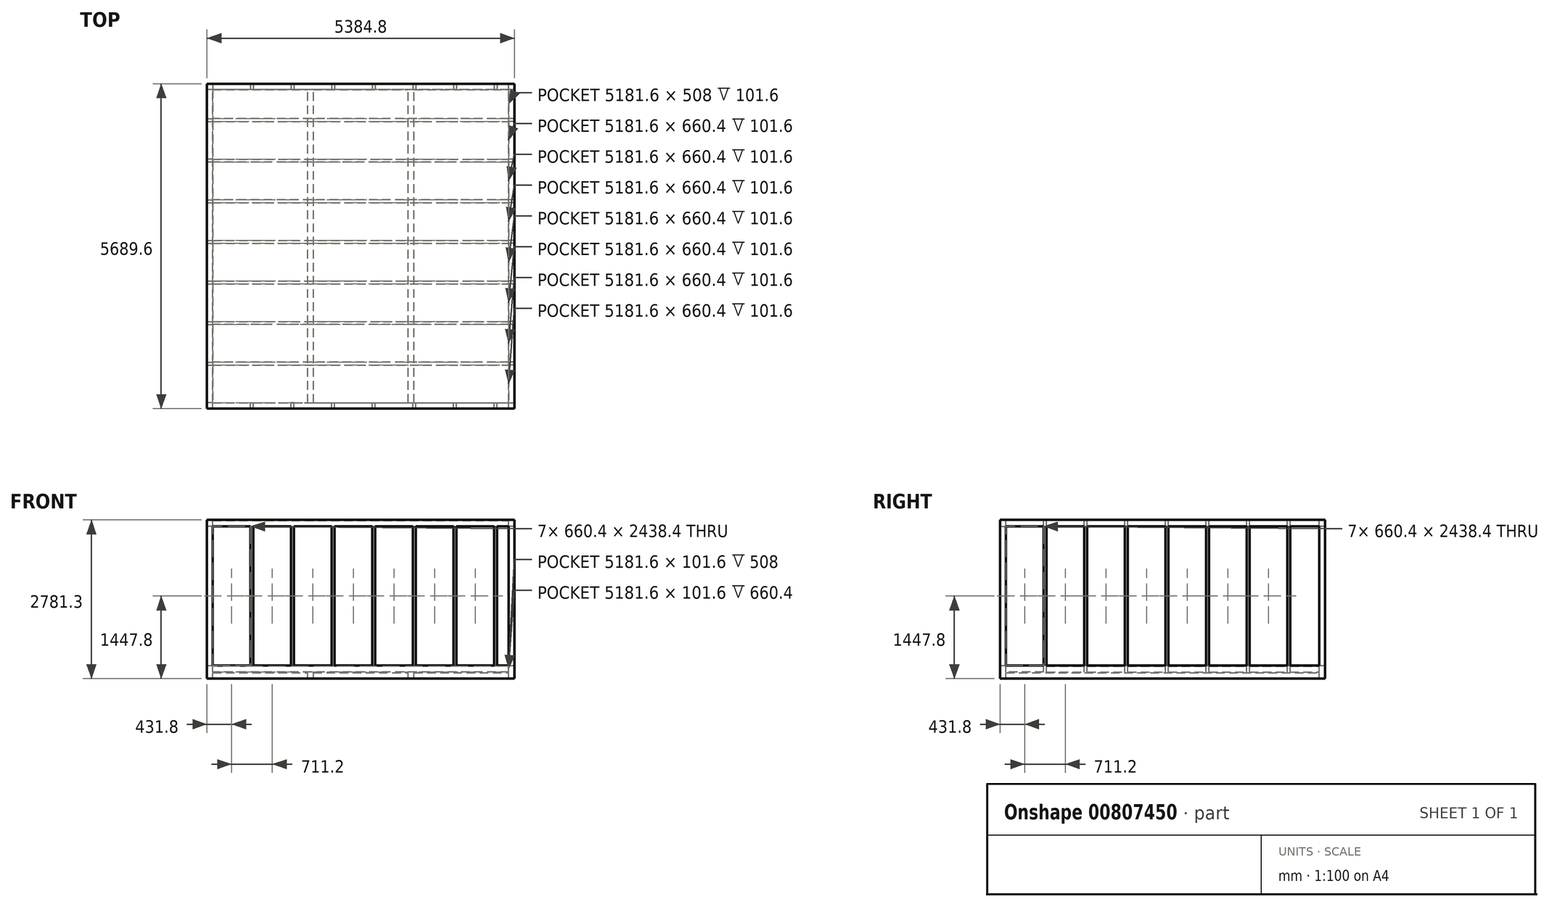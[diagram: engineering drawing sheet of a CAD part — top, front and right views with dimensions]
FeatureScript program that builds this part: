
annotation { "Feature Type Name" : "Feature", "Feature Type Description" : "" }
export const myFeature = defineFeature(function(context is Context, id is Id, definition is map)
    precondition{}
    {
        {
            var Q0;
            Q0=qCreatedBy(makeId("Top.planeOp"),FACE);
            var sketch = newSketch(context, id + "F0", { "sketchPlane" : qUnion([Q0])});
            skLineSegment(sketch, "E0.bottom", {"start": v(0, 0) * mm, "end": v(-5384.8, 0) * mm});
            skLineSegment(sketch, "E0.top", {"start": v(0, 5689.6) * mm, "end": v(-5384.8, 5689.6) * mm});
            skLineSegment(sketch, "E0.left", {"start": v(0, 0) * mm, "end": v(0, 5689.6) * mm});
            skLineSegment(sketch, "E0.right", {"start": v(-5384.8, 0) * mm, "end": v(-5384.8, 5689.6) * mm});
            skLineSegment(sketch, "E1", {"start": v(-5384.8, 0) * mm, "end": v(-5283.2, 0) * mm});
            skLineSegment(sketch, "E2", {"start": v(-5283.2, 0) * mm, "end": v(-5384.8, 0) * mm});
            skLineSegment(sketch, "E3", {"start": v(-5384.8, 0) * mm, "end": v(-5384.8, 101.6) * mm});
            skLineSegment(sketch, "E4", {"start": v(-5384.8, 101.6) * mm, "end": v(-5384.8, 5588) * mm});
            skLineSegment(sketch, "E5", {"start": v(-5384.8, 5588) * mm, "end": v(-5283.2, 5588) * mm});
            skLineSegment(sketch, "E6", {"start": v(-5283.2, 5588) * mm, "end": v(-101.6, 5588) * mm});
            skSolve(sketch);
        }
        {
            var Q0;
            Q0 = qSketchRegion(id + "F0", true);
            extrude(context, id + "F1", {"entities" : qUnion([Q0]), "depth" : 101.6 * mm, "offsetDistance" : 25.4 * mm});
        }
        {
            var Q0;
            Q0=makeQuery(id+"F1.opExtrude","CAP_FACE",FACE,{"disambiguationData":[OSD([sQuery(id+"F0.wireOp",EDGE,"E0.bottom"),sQuery(id+"F0.wireOp",EDGE,"E0.top"),sQuery(id+"F0.wireOp",EDGE,"E0.left"),sQuery(id+"F0.wireOp",EDGE,"E0.right"),sQuery(id+"F0.wireOp",EDGE,"E2"),sQuery(id+"F0.wireOp",EDGE,"E3"),sQuery(id+"F0.wireOp",EDGE,"E4")])],"isStart":false});
            var sketch = newSketch(context, id + "F2", { "sketchPlane" : qUnion([Q0])});
            skLineSegment(sketch, "E7", {"start": v(-5384.8, 0) * mm, "end": v(-5283.2, 0) * mm});
            skLineSegment(sketch, "E8", {"start": v(-5283.2, 0) * mm, "end": v(-3624.58, 0) * mm});
            skLineSegment(sketch, "E9", {"start": v(-3624.58, 0) * mm, "end": v(-3522.98, 0) * mm});
            skLineSegment(sketch, "E10", {"start": v(-3522.98, 0) * mm, "end": v(-1861.82, 0) * mm});
            skLineSegment(sketch, "E11", {"start": v(-1861.82, 0) * mm, "end": v(-1760.22, 0) * mm});
            skLineSegment(sketch, "E12", {"start": v(-1760.22, 0) * mm, "end": v(-101.6, 0) * mm});
            skLineSegment(sketch, "E13", {"start": v(-101.6, 0) * mm, "end": v(0, 0) * mm});
            skLineSegment(sketch, "E14", {"start": v(0, 0) * mm, "end": v(0, 101.6) * mm});
            skLineSegment(sketch, "E15", {"start": v(0, 101.6) * mm, "end": v(0, 1861.82) * mm});
            skLineSegment(sketch, "E16", {"start": v(0, 1861.82) * mm, "end": v(0, 1963.42) * mm});
            skLineSegment(sketch, "E17", {"start": v(0, 1963.42) * mm, "end": v(0, 3726.18) * mm});
            skLineSegment(sketch, "E18", {"start": v(0, 3726.18) * mm, "end": v(0, 3827.78) * mm});
            skLineSegment(sketch, "E19", {"start": v(0, 3827.78) * mm, "end": v(0, 5588) * mm});
            skLineSegment(sketch, "E20", {"start": v(0, 5588) * mm, "end": v(0, 5689.6) * mm});
            skLineSegment(sketch, "E21.bottom", {"start": v(-5283.2, 101.6) * mm, "end": v(-3624.58, 101.6) * mm});
            skLineSegment(sketch, "E21.top", {"start": v(-5283.2, 5588) * mm, "end": v(-3624.58, 5588) * mm});
            skLineSegment(sketch, "E21.left", {"start": v(-5283.2, 101.6) * mm, "end": v(-5283.2, 5588) * mm});
            skLineSegment(sketch, "E21.right", {"start": v(-3624.58, 101.6) * mm, "end": v(-3624.58, 5588) * mm});
            skLineSegment(sketch, "E22.bottom", {"start": v(-3522.98, 101.6) * mm, "end": v(-1861.82, 101.6) * mm});
            skLineSegment(sketch, "E22.top", {"start": v(-3522.98, 5588) * mm, "end": v(-1861.82, 5588) * mm});
            skLineSegment(sketch, "E22.left", {"start": v(-3522.98, 101.6) * mm, "end": v(-3522.98, 5588) * mm});
            skLineSegment(sketch, "E22.right", {"start": v(-1861.82, 101.6) * mm, "end": v(-1861.82, 5588) * mm});
            skLineSegment(sketch, "E23.bottom", {"start": v(-1760.22, 101.6) * mm, "end": v(-101.6, 101.6) * mm});
            skLineSegment(sketch, "E23.top", {"start": v(-1760.22, 5588) * mm, "end": v(-101.6, 5588) * mm});
            skLineSegment(sketch, "E23.left", {"start": v(-1760.22, 101.6) * mm, "end": v(-1760.22, 5588) * mm});
            skLineSegment(sketch, "E23.right", {"start": v(-101.6, 101.6) * mm, "end": v(-101.6, 5588) * mm});
            skSolve(sketch);
        }
        {
            var Q0;
            Q0 = qSketchRegion(id + "F2", true);
            extrude(context, id + "F3", {"entities" : qUnion([Q0]), "operationType" : NewBodyOperationType.REMOVE, "oppositeDirection" : true, "depth" : 101.6 * mm, "offsetDistance" : 25.4 * mm});
        }
        {
            var Q0;
            Q0=makeQuery(id+"F1.opExtrude","CAP_FACE",FACE,{"disambiguationData":[OSD([sQuery(id+"F0.wireOp",EDGE,"E0.bottom"),sQuery(id+"F0.wireOp",EDGE,"E0.top"),sQuery(id+"F0.wireOp",EDGE,"E0.left"),sQuery(id+"F0.wireOp",EDGE,"E0.right"),sQuery(id+"F0.wireOp",EDGE,"E2"),sQuery(id+"F0.wireOp",EDGE,"E3"),sQuery(id+"F0.wireOp",EDGE,"E4")])],"isStart":false});
            var sketch = newSketch(context, id + "F4", { "sketchPlane" : qUnion([Q0])});
            skLineSegment(sketch, "E24.bottom", {"start": v(-5384.8, 0) * mm, "end": v(0, 0) * mm});
            skLineSegment(sketch, "E24.top", {"start": v(-5384.8, 5689.6) * mm, "end": v(0, 5689.6) * mm});
            skLineSegment(sketch, "E24.left", {"start": v(-5384.8, 0) * mm, "end": v(-5384.8, 5689.6) * mm});
            skLineSegment(sketch, "E24.right", {"start": v(0, 0) * mm, "end": v(0, 5689.6) * mm});
            skSolve(sketch);
        }
        {
            var Q0;
            Q0 = qSketchRegion(id + "F4", true);
            extrude(context, id + "F5", {"entities" : qUnion([Q0]), "operationType" : NewBodyOperationType.ADD, "depth" : 114.3 * mm, "offsetDistance" : 25.4 * mm});
        }
        {
            var Q0;
            Q0=makeQuery(id+"F5.opExtrude","CAP_FACE",FACE,{"disambiguationData":[OSD([sQuery(id+"F4.wireOp",EDGE,"E24.bottom"),sQuery(id+"F4.wireOp",EDGE,"E24.top"),sQuery(id+"F4.wireOp",EDGE,"E24.left"),sQuery(id+"F4.wireOp",EDGE,"E24.right")])],"isStart":false});
            var sketch = newSketch(context, id + "F6", { "sketchPlane" : qUnion([Q0])});
            skLineSegment(sketch, "E25", {"start": v(-5384.8, 0) * mm, "end": v(-5283.2, 0) * mm});
            skLineSegment(sketch, "E26", {"start": v(-5283.2, 0) * mm, "end": v(-101.6, 0) * mm});
            skLineSegment(sketch, "E27", {"start": v(-101.6, 0) * mm, "end": v(0, 0) * mm});
            skLineSegment(sketch, "E28", {"start": v(0, 0) * mm, "end": v(0, 101.6) * mm});
            skLineSegment(sketch, "E29", {"start": v(0, 101.6) * mm, "end": v(0, 762) * mm});
            skLineSegment(sketch, "E30", {"start": v(0, 762) * mm, "end": v(0, 812.8) * mm});
            skLineSegment(sketch, "E31", {"start": v(0, 812.8) * mm, "end": v(0, 1473.2) * mm});
            skLineSegment(sketch, "E32", {"start": v(0, 1473.2) * mm, "end": v(0, 1524) * mm});
            skLineSegment(sketch, "E33", {"start": v(0, 1524) * mm, "end": v(0, 2184.4) * mm});
            skLineSegment(sketch, "E34", {"start": v(0, 2184.4) * mm, "end": v(0, 2235.2) * mm});
            skLineSegment(sketch, "E35", {"start": v(0, 2235.2) * mm, "end": v(0, 2895.6) * mm});
            skLineSegment(sketch, "E36", {"start": v(0, 2895.6) * mm, "end": v(0, 2946.4) * mm});
            skLineSegment(sketch, "E37", {"start": v(0, 2946.4) * mm, "end": v(0, 3606.8) * mm});
            skLineSegment(sketch, "E38", {"start": v(0, 3606.8) * mm, "end": v(0, 3657.6) * mm});
            skLineSegment(sketch, "E39", {"start": v(0, 3657.6) * mm, "end": v(0, 4318) * mm});
            skLineSegment(sketch, "E40", {"start": v(0, 4318) * mm, "end": v(0, 4368.8) * mm});
            skLineSegment(sketch, "E41", {"start": v(0, 4368.8) * mm, "end": v(0, 5029.2) * mm});
            skLineSegment(sketch, "E42", {"start": v(0, 5029.2) * mm, "end": v(0, 5080) * mm});
            skLineSegment(sketch, "E43", {"start": v(0, 5080) * mm, "end": v(0, 5588) * mm});
            skLineSegment(sketch, "E44", {"start": v(0, 5588) * mm, "end": v(0, 5689.6) * mm});
            skLineSegment(sketch, "E45.bottom", {"start": v(-101.6, 762) * mm, "end": v(-5283.2, 762) * mm});
            skLineSegment(sketch, "E45.top", {"start": v(-101.6, 101.6) * mm, "end": v(-5283.2, 101.6) * mm});
            skLineSegment(sketch, "E45.left", {"start": v(-101.6, 762) * mm, "end": v(-101.6, 101.6) * mm});
            skLineSegment(sketch, "E45.right", {"start": v(-5283.2, 762) * mm, "end": v(-5283.2, 101.6) * mm});
            skLineSegment(sketch, "E46.bottom", {"start": v(-101.6, 812.8) * mm, "end": v(-5283.2, 812.8) * mm});
            skLineSegment(sketch, "E46.top", {"start": v(-101.6, 1473.2) * mm, "end": v(-5283.2, 1473.2) * mm});
            skLineSegment(sketch, "E46.left", {"start": v(-101.6, 812.8) * mm, "end": v(-101.6, 1473.2) * mm});
            skLineSegment(sketch, "E46.right", {"start": v(-5283.2, 812.8) * mm, "end": v(-5283.2, 1473.2) * mm});
            skLineSegment(sketch, "E47.bottom", {"start": v(-101.6, 1524) * mm, "end": v(-5283.2, 1524) * mm});
            skLineSegment(sketch, "E47.top", {"start": v(-101.6, 2184.4) * mm, "end": v(-5283.2, 2184.4) * mm});
            skLineSegment(sketch, "E47.left", {"start": v(-101.6, 1524) * mm, "end": v(-101.6, 2184.4) * mm});
            skLineSegment(sketch, "E47.right", {"start": v(-5283.2, 1524) * mm, "end": v(-5283.2, 2184.4) * mm});
            skLineSegment(sketch, "E48.bottom", {"start": v(-101.6, 2235.2) * mm, "end": v(-5283.2, 2235.2) * mm});
            skLineSegment(sketch, "E48.top", {"start": v(-101.6, 2895.6) * mm, "end": v(-5283.2, 2895.6) * mm});
            skLineSegment(sketch, "E48.left", {"start": v(-101.6, 2235.2) * mm, "end": v(-101.6, 2895.6) * mm});
            skLineSegment(sketch, "E48.right", {"start": v(-5283.2, 2235.2) * mm, "end": v(-5283.2, 2895.6) * mm});
            skLineSegment(sketch, "E49.bottom", {"start": v(-101.6, 2946.4) * mm, "end": v(-5283.2, 2946.4) * mm});
            skLineSegment(sketch, "E49.top", {"start": v(-101.6, 3606.8) * mm, "end": v(-5283.2, 3606.8) * mm});
            skLineSegment(sketch, "E49.left", {"start": v(-101.6, 2946.4) * mm, "end": v(-101.6, 3606.8) * mm});
            skLineSegment(sketch, "E49.right", {"start": v(-5283.2, 2946.4) * mm, "end": v(-5283.2, 3606.8) * mm});
            skLineSegment(sketch, "E50.bottom", {"start": v(-101.6, 3657.6) * mm, "end": v(-5283.2, 3657.6) * mm});
            skLineSegment(sketch, "E50.top", {"start": v(-101.6, 4318) * mm, "end": v(-5283.2, 4318) * mm});
            skLineSegment(sketch, "E50.left", {"start": v(-101.6, 3657.6) * mm, "end": v(-101.6, 4318) * mm});
            skLineSegment(sketch, "E50.right", {"start": v(-5283.2, 3657.6) * mm, "end": v(-5283.2, 4318) * mm});
            skLineSegment(sketch, "E51.bottom", {"start": v(-101.6, 4368.8) * mm, "end": v(-5283.2, 4368.8) * mm});
            skLineSegment(sketch, "E51.top", {"start": v(-101.6, 5029.2) * mm, "end": v(-5283.2, 5029.2) * mm});
            skLineSegment(sketch, "E51.left", {"start": v(-101.6, 4368.8) * mm, "end": v(-101.6, 5029.2) * mm});
            skLineSegment(sketch, "E51.right", {"start": v(-5283.2, 4368.8) * mm, "end": v(-5283.2, 5029.2) * mm});
            skLineSegment(sketch, "E52.bottom", {"start": v(-101.6, 5080) * mm, "end": v(-5283.2, 5080) * mm});
            skLineSegment(sketch, "E52.top", {"start": v(-101.6, 5588) * mm, "end": v(-5283.2, 5588) * mm});
            skLineSegment(sketch, "E52.left", {"start": v(-101.6, 5080) * mm, "end": v(-101.6, 5588) * mm});
            skLineSegment(sketch, "E52.right", {"start": v(-5283.2, 5080) * mm, "end": v(-5283.2, 5588) * mm});
            skSolve(sketch);
        }
        {
            var Q0;
            Q0 = qSketchRegion(id + "F6", true);
            extrude(context, id + "F7", {"entities" : qUnion([Q0]), "operationType" : NewBodyOperationType.REMOVE, "oppositeDirection" : true, "depth" : 101.6 * mm, "offsetDistance" : 25.4 * mm});
        }
        {
            var Q0;
            Q0=makeQuery(id+"F5.opExtrude","CAP_FACE",FACE,{"disambiguationData":[OSD([sQuery(id+"F4.wireOp",EDGE,"E24.bottom"),sQuery(id+"F4.wireOp",EDGE,"E24.top"),sQuery(id+"F4.wireOp",EDGE,"E24.left"),sQuery(id+"F4.wireOp",EDGE,"E24.right")])],"isStart":false});
            var sketch = newSketch(context, id + "F8", { "sketchPlane" : qUnion([Q0])});
            skLineSegment(sketch, "E53.bottom", {"start": v(-5384.8, 5689.6) * mm, "end": v(0, 5689.6) * mm});
            skLineSegment(sketch, "E53.top", {"start": v(-5384.8, 0) * mm, "end": v(0, 0) * mm});
            skLineSegment(sketch, "E53.left", {"start": v(-5384.8, 5689.6) * mm, "end": v(-5384.8, 0) * mm});
            skLineSegment(sketch, "E53.right", {"start": v(0, 5689.6) * mm, "end": v(0, 0) * mm});
            skSolve(sketch);
        }
        {
            var Q0;
            Q0 = qSketchRegion(id + "F8", true);
            extrude(context, id + "F9", {"entities" : qUnion([Q0]), "operationType" : NewBodyOperationType.ADD, "depth" : 12.7 * mm, "offsetDistance" : 25.4 * mm});
        }
        {
            var Q0;
            Q0=makeQuery(id+"F9.opExtrude","CAP_FACE",FACE,{"disambiguationData":[OSD([sQuery(id+"F8.wireOp",EDGE,"E53.bottom"),sQuery(id+"F8.wireOp",EDGE,"E53.top"),sQuery(id+"F8.wireOp",EDGE,"E53.left"),sQuery(id+"F8.wireOp",EDGE,"E53.right")])],"isStart":false});
            var sketch = newSketch(context, id + "F10", { "sketchPlane" : qUnion([Q0])});
            skLineSegment(sketch, "E54", {"start": v(-5384.8, 0) * mm, "end": v(-5283.2, 0) * mm});
            skLineSegment(sketch, "E55", {"start": v(-5283.2, 0) * mm, "end": v(-4622.8, 0) * mm});
            skLineSegment(sketch, "E56", {"start": v(-4622.8, 0) * mm, "end": v(-4572, 0) * mm});
            skLineSegment(sketch, "E57", {"start": v(-4572, 0) * mm, "end": v(-3911.6, 0) * mm});
            skLineSegment(sketch, "E58", {"start": v(-3911.6, 0) * mm, "end": v(-3860.8, 0) * mm});
            skLineSegment(sketch, "E59", {"start": v(-3860.8, 0) * mm, "end": v(-3200.4, 0) * mm});
            skLineSegment(sketch, "E60", {"start": v(-101.6, 0) * mm, "end": v(0, 0) * mm});
            skLineSegment(sketch, "E61", {"start": v(0, 0) * mm, "end": v(0, 101.6) * mm});
            skLineSegment(sketch, "E62", {"start": v(0, 101.6) * mm, "end": v(0, 762) * mm});
            skLineSegment(sketch, "E63", {"start": v(0, 762) * mm, "end": v(0, 812.8) * mm});
            skLineSegment(sketch, "E64", {"start": v(0, 812.8) * mm, "end": v(0, 1473.2) * mm});
            skLineSegment(sketch, "E65", {"start": v(0, 1473.2) * mm, "end": v(0, 1524) * mm});
            skLineSegment(sketch, "E66", {"start": v(0, 1524) * mm, "end": v(0, 2184.4) * mm});
            skLineSegment(sketch, "E67", {"start": v(0, 2184.4) * mm, "end": v(0, 2235.2) * mm});
            skLineSegment(sketch, "E68", {"start": v(0, 2235.2) * mm, "end": v(0, 2895.6) * mm});
            skLineSegment(sketch, "E69", {"start": v(0, 2895.6) * mm, "end": v(0, 2946.4) * mm});
            skLineSegment(sketch, "E70", {"start": v(0, 2946.4) * mm, "end": v(0, 3606.8) * mm});
            skLineSegment(sketch, "E71", {"start": v(0, 3606.8) * mm, "end": v(0, 3657.6) * mm});
            skLineSegment(sketch, "E72", {"start": v(0, 3657.6) * mm, "end": v(0, 4318) * mm});
            skLineSegment(sketch, "E73", {"start": v(0, 4318) * mm, "end": v(0, 4368.8) * mm});
            skLineSegment(sketch, "E74", {"start": v(0, 4368.8) * mm, "end": v(0, 5029.2) * mm});
            skLineSegment(sketch, "E75", {"start": v(0, 5029.2) * mm, "end": v(0, 5080) * mm});
            skLineSegment(sketch, "E76", {"start": v(0, 5080) * mm, "end": v(0, 5588) * mm});
            skLineSegment(sketch, "E77", {"start": v(0, 5588) * mm, "end": v(0, 5689.6) * mm});
            skLineSegment(sketch, "E78.bottom", {"start": v(-5283.2, 0) * mm, "end": v(-5384.8, 0) * mm});
            skLineSegment(sketch, "E78.top", {"start": v(-5283.2, 101.6) * mm, "end": v(-5384.8, 101.6) * mm});
            skLineSegment(sketch, "E78.left", {"start": v(-5283.2, 0) * mm, "end": v(-5283.2, 101.6) * mm});
            skLineSegment(sketch, "E78.right", {"start": v(-5384.8, 0) * mm, "end": v(-5384.8, 101.6) * mm});
            skLineSegment(sketch, "E79.top", {"start": v(-4622.8, 101.6) * mm, "end": v(-4572, 101.6) * mm});
            skLineSegment(sketch, "E79.left", {"start": v(-4622.8, 0) * mm, "end": v(-4622.8, 101.6) * mm});
            skLineSegment(sketch, "E79.right", {"start": v(-4572, 0) * mm, "end": v(-4572, 101.6) * mm});
            skLineSegment(sketch, "E80.bottom", {"start": v(-3860.8, 0) * mm, "end": v(-3911.6, 0) * mm});
            skLineSegment(sketch, "E80.top", {"start": v(-3860.8, 101.6) * mm, "end": v(-3911.6, 101.6) * mm});
            skLineSegment(sketch, "E80.left", {"start": v(-3860.8, 0) * mm, "end": v(-3860.8, 101.6) * mm});
            skLineSegment(sketch, "E80.right", {"start": v(-3911.6, 0) * mm, "end": v(-3911.6, 101.6) * mm});
            skLineSegment(sketch, "E81", {"start": v(-3200.4, 0) * mm, "end": v(-3149.6, 0) * mm});
            skLineSegment(sketch, "E82", {"start": v(-3149.6, 0) * mm, "end": v(-2489.2, 0) * mm});
            skLineSegment(sketch, "E83", {"start": v(-2489.2, 0) * mm, "end": v(-2438.4, 0) * mm});
            skLineSegment(sketch, "E84", {"start": v(-2438.4, 0) * mm, "end": v(-1778, 0) * mm});
            skLineSegment(sketch, "E85", {"start": v(-1778, 0) * mm, "end": v(-1727.2, 0) * mm});
            skLineSegment(sketch, "E86", {"start": v(-1727.2, 0) * mm, "end": v(-1066.8, 0) * mm});
            skLineSegment(sketch, "E87", {"start": v(-1066.8, 0) * mm, "end": v(-1016, 0) * mm});
            skLineSegment(sketch, "E88", {"start": v(-1016, 0) * mm, "end": v(-355.6, 0) * mm});
            skLineSegment(sketch, "E89", {"start": v(-355.6, 0) * mm, "end": v(-304.8, 0) * mm});
            skLineSegment(sketch, "E90", {"start": v(-304.8, 0) * mm, "end": v(-101.6, 0) * mm});
            skLineSegment(sketch, "E91.top", {"start": v(-3200.4, 101.6) * mm, "end": v(-3149.6, 101.6) * mm});
            skLineSegment(sketch, "E91.left", {"start": v(-3200.4, 0) * mm, "end": v(-3200.4, 101.6) * mm});
            skLineSegment(sketch, "E91.right", {"start": v(-3149.6, 0) * mm, "end": v(-3149.6, 101.6) * mm});
            skLineSegment(sketch, "E92.top", {"start": v(-2489.2, 101.6) * mm, "end": v(-2438.4, 101.6) * mm});
            skLineSegment(sketch, "E92.left", {"start": v(-2489.2, 0) * mm, "end": v(-2489.2, 101.6) * mm});
            skLineSegment(sketch, "E92.right", {"start": v(-2438.4, 0) * mm, "end": v(-2438.4, 101.6) * mm});
            skLineSegment(sketch, "E93.top", {"start": v(-1778, 101.6) * mm, "end": v(-1727.2, 101.6) * mm});
            skLineSegment(sketch, "E93.left", {"start": v(-1778, 0) * mm, "end": v(-1778, 101.6) * mm});
            skLineSegment(sketch, "E93.right", {"start": v(-1727.2, 0) * mm, "end": v(-1727.2, 101.6) * mm});
            skLineSegment(sketch, "E94.top", {"start": v(-1066.8, 101.6) * mm, "end": v(-1016, 101.6) * mm});
            skLineSegment(sketch, "E94.left", {"start": v(-1066.8, 0) * mm, "end": v(-1066.8, 101.6) * mm});
            skLineSegment(sketch, "E94.right", {"start": v(-1016, 0) * mm, "end": v(-1016, 101.6) * mm});
            skLineSegment(sketch, "E95.top", {"start": v(-355.6, 101.6) * mm, "end": v(-304.8, 101.6) * mm});
            skLineSegment(sketch, "E95.left", {"start": v(-355.6, 0) * mm, "end": v(-355.6, 101.6) * mm});
            skLineSegment(sketch, "E95.right", {"start": v(-304.8, 0) * mm, "end": v(-304.8, 101.6) * mm});
            skLineSegment(sketch, "E96.top", {"start": v(-101.6, 101.6) * mm, "end": v(0, 101.6) * mm});
            skLineSegment(sketch, "E96.left", {"start": v(-101.6, 0) * mm, "end": v(-101.6, 101.6) * mm});
            skLineSegment(sketch, "E97.bottom", {"start": v(0, 762) * mm, "end": v(-101.6, 762) * mm});
            skLineSegment(sketch, "E97.top", {"start": v(0, 812.8) * mm, "end": v(-101.6, 812.8) * mm});
            skLineSegment(sketch, "E97.right", {"start": v(-101.6, 762) * mm, "end": v(-101.6, 812.8) * mm});
            skLineSegment(sketch, "E98.bottom", {"start": v(0, 1473.2) * mm, "end": v(-101.6, 1473.2) * mm});
            skLineSegment(sketch, "E98.top", {"start": v(0, 1524) * mm, "end": v(-101.6, 1524) * mm});
            skLineSegment(sketch, "E98.right", {"start": v(-101.6, 1473.2) * mm, "end": v(-101.6, 1524) * mm});
            skLineSegment(sketch, "E99.bottom", {"start": v(0, 2184.4) * mm, "end": v(-101.6, 2184.4) * mm});
            skLineSegment(sketch, "E99.top", {"start": v(0, 2235.2) * mm, "end": v(-101.6, 2235.2) * mm});
            skLineSegment(sketch, "E99.right", {"start": v(-101.6, 2184.4) * mm, "end": v(-101.6, 2235.2) * mm});
            skLineSegment(sketch, "E100.bottom", {"start": v(0, 2895.6) * mm, "end": v(-101.6, 2895.6) * mm});
            skLineSegment(sketch, "E100.top", {"start": v(0, 2946.4) * mm, "end": v(-101.6, 2946.4) * mm});
            skLineSegment(sketch, "E100.right", {"start": v(-101.6, 2895.6) * mm, "end": v(-101.6, 2946.4) * mm});
            skLineSegment(sketch, "E101.bottom", {"start": v(0, 3606.8) * mm, "end": v(-101.6, 3606.8) * mm});
            skLineSegment(sketch, "E101.top", {"start": v(0, 3657.6) * mm, "end": v(-101.6, 3657.6) * mm});
            skLineSegment(sketch, "E101.right", {"start": v(-101.6, 3606.8) * mm, "end": v(-101.6, 3657.6) * mm});
            skLineSegment(sketch, "E102.bottom", {"start": v(0, 4318) * mm, "end": v(-101.6, 4318) * mm});
            skLineSegment(sketch, "E102.top", {"start": v(0, 4368.8) * mm, "end": v(-101.6, 4368.8) * mm});
            skLineSegment(sketch, "E102.right", {"start": v(-101.6, 4318) * mm, "end": v(-101.6, 4368.8) * mm});
            skLineSegment(sketch, "E103.bottom", {"start": v(0, 5029.2) * mm, "end": v(-101.6, 5029.2) * mm});
            skLineSegment(sketch, "E103.top", {"start": v(0, 5080) * mm, "end": v(-101.6, 5080) * mm});
            skLineSegment(sketch, "E103.right", {"start": v(-101.6, 5029.2) * mm, "end": v(-101.6, 5080) * mm});
            skLineSegment(sketch, "E104.bottom", {"start": v(0, 5588) * mm, "end": v(-101.6, 5588) * mm});
            skLineSegment(sketch, "E104.top", {"start": v(0, 5689.6) * mm, "end": v(-101.6, 5689.6) * mm});
            skLineSegment(sketch, "E104.right", {"start": v(-101.6, 5588) * mm, "end": v(-101.6, 5689.6) * mm});
            skLineSegment(sketch, "E105.bottom", {"start": v(-304.8, 5689.6) * mm, "end": v(-355.6, 5689.6) * mm});
            skLineSegment(sketch, "E105.top", {"start": v(-304.8, 5588) * mm, "end": v(-355.6, 5588) * mm});
            skLineSegment(sketch, "E105.left", {"start": v(-304.8, 5689.6) * mm, "end": v(-304.8, 5588) * mm});
            skLineSegment(sketch, "E105.right", {"start": v(-355.6, 5689.6) * mm, "end": v(-355.6, 5588) * mm});
            skLineSegment(sketch, "E106.bottom", {"start": v(-1016, 5689.6) * mm, "end": v(-1066.8, 5689.6) * mm});
            skLineSegment(sketch, "E106.top", {"start": v(-1016, 5588) * mm, "end": v(-1066.8, 5588) * mm});
            skLineSegment(sketch, "E106.left", {"start": v(-1016, 5689.6) * mm, "end": v(-1016, 5588) * mm});
            skLineSegment(sketch, "E106.right", {"start": v(-1066.8, 5689.6) * mm, "end": v(-1066.8, 5588) * mm});
            skLineSegment(sketch, "E107.bottom", {"start": v(-1727.2, 5689.6) * mm, "end": v(-1778, 5689.6) * mm});
            skLineSegment(sketch, "E107.top", {"start": v(-1727.2, 5588) * mm, "end": v(-1778, 5588) * mm});
            skLineSegment(sketch, "E107.left", {"start": v(-1727.2, 5689.6) * mm, "end": v(-1727.2, 5588) * mm});
            skLineSegment(sketch, "E107.right", {"start": v(-1778, 5689.6) * mm, "end": v(-1778, 5588) * mm});
            skLineSegment(sketch, "E108.bottom", {"start": v(-2438.4, 5689.6) * mm, "end": v(-2489.2, 5689.6) * mm});
            skLineSegment(sketch, "E108.top", {"start": v(-2438.4, 5588) * mm, "end": v(-2489.2, 5588) * mm});
            skLineSegment(sketch, "E108.left", {"start": v(-2438.4, 5689.6) * mm, "end": v(-2438.4, 5588) * mm});
            skLineSegment(sketch, "E108.right", {"start": v(-2489.2, 5689.6) * mm, "end": v(-2489.2, 5588) * mm});
            skLineSegment(sketch, "E109.bottom", {"start": v(-3149.6, 5689.6) * mm, "end": v(-3200.4, 5689.6) * mm});
            skLineSegment(sketch, "E109.top", {"start": v(-3149.6, 5588) * mm, "end": v(-3200.4, 5588) * mm});
            skLineSegment(sketch, "E109.left", {"start": v(-3149.6, 5689.6) * mm, "end": v(-3149.6, 5588) * mm});
            skLineSegment(sketch, "E109.right", {"start": v(-3200.4, 5689.6) * mm, "end": v(-3200.4, 5588) * mm});
            skLineSegment(sketch, "E110.bottom", {"start": v(-3860.8, 5689.6) * mm, "end": v(-3911.6, 5689.6) * mm});
            skLineSegment(sketch, "E110.top", {"start": v(-3860.8, 5588) * mm, "end": v(-3911.6, 5588) * mm});
            skLineSegment(sketch, "E110.left", {"start": v(-3860.8, 5689.6) * mm, "end": v(-3860.8, 5588) * mm});
            skLineSegment(sketch, "E110.right", {"start": v(-3911.6, 5689.6) * mm, "end": v(-3911.6, 5588) * mm});
            skLineSegment(sketch, "E111.bottom", {"start": v(-4572, 5689.6) * mm, "end": v(-4622.8, 5689.6) * mm});
            skLineSegment(sketch, "E111.top", {"start": v(-4572, 5588) * mm, "end": v(-4622.8, 5588) * mm});
            skLineSegment(sketch, "E111.left", {"start": v(-4572, 5689.6) * mm, "end": v(-4572, 5588) * mm});
            skLineSegment(sketch, "E111.right", {"start": v(-4622.8, 5689.6) * mm, "end": v(-4622.8, 5588) * mm});
            skLineSegment(sketch, "E112.bottom", {"start": v(-5283.2, 5689.6) * mm, "end": v(-5384.8, 5689.6) * mm});
            skLineSegment(sketch, "E112.top", {"start": v(-5283.2, 5588) * mm, "end": v(-5384.8, 5588) * mm});
            skLineSegment(sketch, "E112.left", {"start": v(-5283.2, 5689.6) * mm, "end": v(-5283.2, 5588) * mm});
            skLineSegment(sketch, "E112.right", {"start": v(-5384.8, 5689.6) * mm, "end": v(-5384.8, 5588) * mm});
            skLineSegment(sketch, "E113.bottom", {"start": v(-5384.8, 5080) * mm, "end": v(-5283.2, 5080) * mm});
            skLineSegment(sketch, "E113.top", {"start": v(-5384.8, 5029.2) * mm, "end": v(-5283.2, 5029.2) * mm});
            skLineSegment(sketch, "E113.left", {"start": v(-5384.8, 5080) * mm, "end": v(-5384.8, 5029.2) * mm});
            skLineSegment(sketch, "E113.right", {"start": v(-5283.2, 5080) * mm, "end": v(-5283.2, 5029.2) * mm});
            skLineSegment(sketch, "E114.bottom", {"start": v(-5283.2, 4368.8) * mm, "end": v(-5384.8, 4368.8) * mm});
            skLineSegment(sketch, "E114.top", {"start": v(-5283.2, 4318) * mm, "end": v(-5384.8, 4318) * mm});
            skLineSegment(sketch, "E114.left", {"start": v(-5283.2, 4368.8) * mm, "end": v(-5283.2, 4318) * mm});
            skLineSegment(sketch, "E114.right", {"start": v(-5384.8, 4368.8) * mm, "end": v(-5384.8, 4318) * mm});
            skLineSegment(sketch, "E115.bottom", {"start": v(-5384.8, 3657.6) * mm, "end": v(-5283.2, 3657.6) * mm});
            skLineSegment(sketch, "E115.top", {"start": v(-5384.8, 3606.8) * mm, "end": v(-5283.2, 3606.8) * mm});
            skLineSegment(sketch, "E115.left", {"start": v(-5384.8, 3657.6) * mm, "end": v(-5384.8, 3606.8) * mm});
            skLineSegment(sketch, "E115.right", {"start": v(-5283.2, 3657.6) * mm, "end": v(-5283.2, 3606.8) * mm});
            skLineSegment(sketch, "E116.bottom", {"start": v(-5384.8, 2946.4) * mm, "end": v(-5283.2, 2946.4) * mm});
            skLineSegment(sketch, "E116.top", {"start": v(-5384.8, 2895.6) * mm, "end": v(-5283.2, 2895.6) * mm});
            skLineSegment(sketch, "E116.left", {"start": v(-5384.8, 2946.4) * mm, "end": v(-5384.8, 2895.6) * mm});
            skLineSegment(sketch, "E116.right", {"start": v(-5283.2, 2946.4) * mm, "end": v(-5283.2, 2895.6) * mm});
            skLineSegment(sketch, "E117.bottom", {"start": v(-5384.8, 2235.2) * mm, "end": v(-5283.2, 2235.2) * mm});
            skLineSegment(sketch, "E117.top", {"start": v(-5384.8, 2184.4) * mm, "end": v(-5283.2, 2184.4) * mm});
            skLineSegment(sketch, "E117.left", {"start": v(-5384.8, 2235.2) * mm, "end": v(-5384.8, 2184.4) * mm});
            skLineSegment(sketch, "E117.right", {"start": v(-5283.2, 2235.2) * mm, "end": v(-5283.2, 2184.4) * mm});
            skLineSegment(sketch, "E118.bottom", {"start": v(-5384.8, 1473.2) * mm, "end": v(-5283.2, 1473.2) * mm});
            skLineSegment(sketch, "E118.top", {"start": v(-5384.8, 1524) * mm, "end": v(-5283.2, 1524) * mm});
            skLineSegment(sketch, "E118.left", {"start": v(-5384.8, 1473.2) * mm, "end": v(-5384.8, 1524) * mm});
            skLineSegment(sketch, "E118.right", {"start": v(-5283.2, 1473.2) * mm, "end": v(-5283.2, 1524) * mm});
            skLineSegment(sketch, "E119.bottom", {"start": v(-5384.8, 812.8) * mm, "end": v(-5283.2, 812.8) * mm});
            skLineSegment(sketch, "E119.top", {"start": v(-5384.8, 762) * mm, "end": v(-5283.2, 762) * mm});
            skLineSegment(sketch, "E119.left", {"start": v(-5384.8, 812.8) * mm, "end": v(-5384.8, 762) * mm});
            skLineSegment(sketch, "E119.right", {"start": v(-5283.2, 812.8) * mm, "end": v(-5283.2, 762) * mm});
            skSolve(sketch);
        }
        {
            var Q0;
            Q0 = qSketchRegion(id + "F10", true);
            extrude(context, id + "F11", {"entities" : qUnion([Q0]), "operationType" : NewBodyOperationType.ADD, "depth" : 2438.4 * mm, "offsetDistance" : 25.4 * mm});
        }
        {
            var Q0;
            Q0=makeQuery(id+"F11.opExtrude","CAP_FACE",FACE,{"disambiguationData":[OSD([sQuery(id+"F10.wireOp",EDGE,"E78.bottom"),sQuery(id+"F10.wireOp",EDGE,"E78.top"),sQuery(id+"F10.wireOp",EDGE,"E78.left"),sQuery(id+"F10.wireOp",EDGE,"E78.right")])],"isStart":false});
            var sketch = newSketch(context, id + "F12", { "sketchPlane" : qUnion([Q0])});
            skLineSegment(sketch, "E120.bottom", {"start": v(-5384.8, 0) * mm, "end": v(0, 0) * mm});
            skLineSegment(sketch, "E120.top", {"start": v(-5384.8, 5689.6) * mm, "end": v(0, 5689.6) * mm});
            skLineSegment(sketch, "E120.left", {"start": v(-5384.8, 0) * mm, "end": v(-5384.8, 5689.6) * mm});
            skLineSegment(sketch, "E120.right", {"start": v(0, 0) * mm, "end": v(0, 5689.6) * mm});
            skSolve(sketch);
        }
        {
            var Q0;
            Q0 = qSketchRegion(id + "F12", true);
            extrude(context, id + "F13", {"entities" : qUnion([Q0]), "operationType" : NewBodyOperationType.ADD, "depth" : 101.6 * mm, "offsetDistance" : 25.4 * mm});
        }
        {
            var Q0;
            Q0=makeQuery(id+"F13.opExtrude","CAP_FACE",FACE,{"disambiguationData":[OSD([sQuery(id+"F12.wireOp",EDGE,"E120.bottom"),sQuery(id+"F12.wireOp",EDGE,"E120.top"),sQuery(id+"F12.wireOp",EDGE,"E120.left"),sQuery(id+"F12.wireOp",EDGE,"E120.right")])],"isStart":false});
            var sketch = newSketch(context, id + "F14", { "sketchPlane" : qUnion([Q0])});
            skLineSegment(sketch, "E121", {"start": v(-5384.8, 0) * mm, "end": v(-5283.2, 0) * mm});
            skLineSegment(sketch, "E122", {"start": v(-5283.2, 0) * mm, "end": v(-4622.8, 0) * mm});
            skLineSegment(sketch, "E123", {"start": v(-4622.8, 0) * mm, "end": v(-4572, 0) * mm});
            skLineSegment(sketch, "E124", {"start": v(-4572, 0) * mm, "end": v(-3911.6, 0) * mm});
            skLineSegment(sketch, "E125", {"start": v(-3911.6, 0) * mm, "end": v(-3860.8, 0) * mm});
            skLineSegment(sketch, "E126", {"start": v(-3860.8, 0) * mm, "end": v(-3200.4, 0) * mm});
            skLineSegment(sketch, "E127", {"start": v(-3200.4, 0) * mm, "end": v(-101.6, 0) * mm});
            skLineSegment(sketch, "E128", {"start": v(-101.6, 0) * mm, "end": v(0, 0) * mm});
            skLineSegment(sketch, "E129", {"start": v(0, 0) * mm, "end": v(0, 101.6) * mm});
            skLineSegment(sketch, "E130", {"start": v(0, 101.6) * mm, "end": v(0, 762) * mm});
            skLineSegment(sketch, "E131", {"start": v(0, 762) * mm, "end": v(0, 812.8) * mm});
            skLineSegment(sketch, "E132", {"start": v(0, 812.8) * mm, "end": v(0, 1473.2) * mm});
            skLineSegment(sketch, "E133", {"start": v(0, 1473.2) * mm, "end": v(0, 1524) * mm});
            skLineSegment(sketch, "E134", {"start": v(0, 1524) * mm, "end": v(0, 2184.4) * mm});
            skLineSegment(sketch, "E135", {"start": v(0, 2184.4) * mm, "end": v(0, 2235.2) * mm});
            skLineSegment(sketch, "E136", {"start": v(0, 2235.2) * mm, "end": v(0, 2895.6) * mm});
            skLineSegment(sketch, "E137", {"start": v(0, 2895.6) * mm, "end": v(0, 2946.4) * mm});
            skLineSegment(sketch, "E138", {"start": v(0, 2946.4) * mm, "end": v(0, 3606.8) * mm});
            skLineSegment(sketch, "E139", {"start": v(0, 3606.8) * mm, "end": v(0, 3657.6) * mm});
            skLineSegment(sketch, "E140", {"start": v(0, 3657.6) * mm, "end": v(0, 4318) * mm});
            skLineSegment(sketch, "E141", {"start": v(0, 4318) * mm, "end": v(0, 4368.8) * mm});
            skLineSegment(sketch, "E142", {"start": v(0, 4368.8) * mm, "end": v(0, 5029.2) * mm});
            skLineSegment(sketch, "E143", {"start": v(0, 5029.2) * mm, "end": v(0, 5080) * mm});
            skLineSegment(sketch, "E144", {"start": v(0, 5080) * mm, "end": v(0, 5588) * mm});
            skLineSegment(sketch, "E145", {"start": v(0, 5588) * mm, "end": v(0, 5689.6) * mm});
            skLineSegment(sketch, "E146.bottom", {"start": v(-101.6, 5588) * mm, "end": v(-5283.2, 5588) * mm});
            skLineSegment(sketch, "E146.top", {"start": v(-101.6, 5080) * mm, "end": v(-5283.2, 5080) * mm});
            skLineSegment(sketch, "E146.left", {"start": v(-101.6, 5588) * mm, "end": v(-101.6, 5080) * mm});
            skLineSegment(sketch, "E146.right", {"start": v(-5283.2, 5588) * mm, "end": v(-5283.2, 5080) * mm});
            skLineSegment(sketch, "E147.bottom", {"start": v(-5283.2, 5029.2) * mm, "end": v(-101.6, 5029.2) * mm});
            skLineSegment(sketch, "E147.top", {"start": v(-5283.2, 4368.8) * mm, "end": v(-101.6, 4368.8) * mm});
            skLineSegment(sketch, "E147.left", {"start": v(-5283.2, 5029.2) * mm, "end": v(-5283.2, 4368.8) * mm});
            skLineSegment(sketch, "E147.right", {"start": v(-101.6, 5029.2) * mm, "end": v(-101.6, 4368.8) * mm});
            skLineSegment(sketch, "E148.bottom", {"start": v(-101.6, 4318) * mm, "end": v(-5283.2, 4318) * mm});
            skLineSegment(sketch, "E148.top", {"start": v(-101.6, 3657.6) * mm, "end": v(-5283.2, 3657.6) * mm});
            skLineSegment(sketch, "E148.left", {"start": v(-101.6, 4318) * mm, "end": v(-101.6, 3657.6) * mm});
            skLineSegment(sketch, "E148.right", {"start": v(-5283.2, 4318) * mm, "end": v(-5283.2, 3657.6) * mm});
            skLineSegment(sketch, "E149.bottom", {"start": v(-5283.2, 3606.8) * mm, "end": v(-101.6, 3606.8) * mm});
            skLineSegment(sketch, "E149.top", {"start": v(-5283.2, 2946.4) * mm, "end": v(-101.6, 2946.4) * mm});
            skLineSegment(sketch, "E149.left", {"start": v(-5283.2, 3606.8) * mm, "end": v(-5283.2, 2946.4) * mm});
            skLineSegment(sketch, "E149.right", {"start": v(-101.6, 3606.8) * mm, "end": v(-101.6, 2946.4) * mm});
            skLineSegment(sketch, "E150.bottom", {"start": v(-5283.2, 2895.6) * mm, "end": v(-101.6, 2895.6) * mm});
            skLineSegment(sketch, "E150.top", {"start": v(-5283.2, 2235.2) * mm, "end": v(-101.6, 2235.2) * mm});
            skLineSegment(sketch, "E150.left", {"start": v(-5283.2, 2895.6) * mm, "end": v(-5283.2, 2235.2) * mm});
            skLineSegment(sketch, "E150.right", {"start": v(-101.6, 2895.6) * mm, "end": v(-101.6, 2235.2) * mm});
            skLineSegment(sketch, "E151.bottom", {"start": v(-5283.2, 2184.4) * mm, "end": v(-101.6, 2184.4) * mm});
            skLineSegment(sketch, "E151.top", {"start": v(-5283.2, 1524) * mm, "end": v(-101.6, 1524) * mm});
            skLineSegment(sketch, "E151.left", {"start": v(-5283.2, 2184.4) * mm, "end": v(-5283.2, 1524) * mm});
            skLineSegment(sketch, "E151.right", {"start": v(-101.6, 2184.4) * mm, "end": v(-101.6, 1524) * mm});
            skLineSegment(sketch, "E152.bottom", {"start": v(-101.6, 1473.2) * mm, "end": v(-5283.2, 1473.2) * mm});
            skLineSegment(sketch, "E152.top", {"start": v(-101.6, 812.8) * mm, "end": v(-5283.2, 812.8) * mm});
            skLineSegment(sketch, "E152.left", {"start": v(-101.6, 1473.2) * mm, "end": v(-101.6, 812.8) * mm});
            skLineSegment(sketch, "E152.right", {"start": v(-5283.2, 1473.2) * mm, "end": v(-5283.2, 812.8) * mm});
            skLineSegment(sketch, "E153.bottom", {"start": v(-5283.2, 762) * mm, "end": v(-101.6, 762) * mm});
            skLineSegment(sketch, "E153.top", {"start": v(-5283.2, 101.6) * mm, "end": v(-101.6, 101.6) * mm});
            skLineSegment(sketch, "E153.left", {"start": v(-5283.2, 762) * mm, "end": v(-5283.2, 101.6) * mm});
            skLineSegment(sketch, "E153.right", {"start": v(-101.6, 762) * mm, "end": v(-101.6, 101.6) * mm});
            skSolve(sketch);
        }
        {
            var Q0;
            Q0 = qSketchRegion(id + "F14", true);
            extrude(context, id + "F15", {"entities" : qUnion([Q0]), "operationType" : NewBodyOperationType.REMOVE, "oppositeDirection" : true, "depth" : 101.6 * mm, "offsetDistance" : 25.4 * mm});
        }
        {
            var Q0;
            Q0=makeQuery(id+"F13.opExtrude","CAP_FACE",FACE,{"disambiguationData":[OSD([sQuery(id+"F12.wireOp",EDGE,"E120.bottom"),sQuery(id+"F12.wireOp",EDGE,"E120.top"),sQuery(id+"F12.wireOp",EDGE,"E120.left"),sQuery(id+"F12.wireOp",EDGE,"E120.right")])],"isStart":false});
            var sketch = newSketch(context, id + "F16", { "sketchPlane" : qUnion([Q0])});
            skLineSegment(sketch, "E154.bottom", {"start": v(-5384.8, 5689.6) * mm, "end": v(0, 5689.6) * mm});
            skLineSegment(sketch, "E154.top", {"start": v(-5384.8, 0) * mm, "end": v(0, 0) * mm});
            skLineSegment(sketch, "E154.left", {"start": v(-5384.8, 5689.6) * mm, "end": v(-5384.8, 0) * mm});
            skLineSegment(sketch, "E154.right", {"start": v(0, 5689.6) * mm, "end": v(0, 0) * mm});
            skSolve(sketch);
        }
        {
            var Q0;
            Q0 = qSketchRegion(id + "F16", true);
            extrude(context, id + "F17", {"entities" : qUnion([Q0]), "operationType" : NewBodyOperationType.ADD, "depth" : 12.7 * mm, "offsetDistance" : 25.4 * mm});
        }
    });
